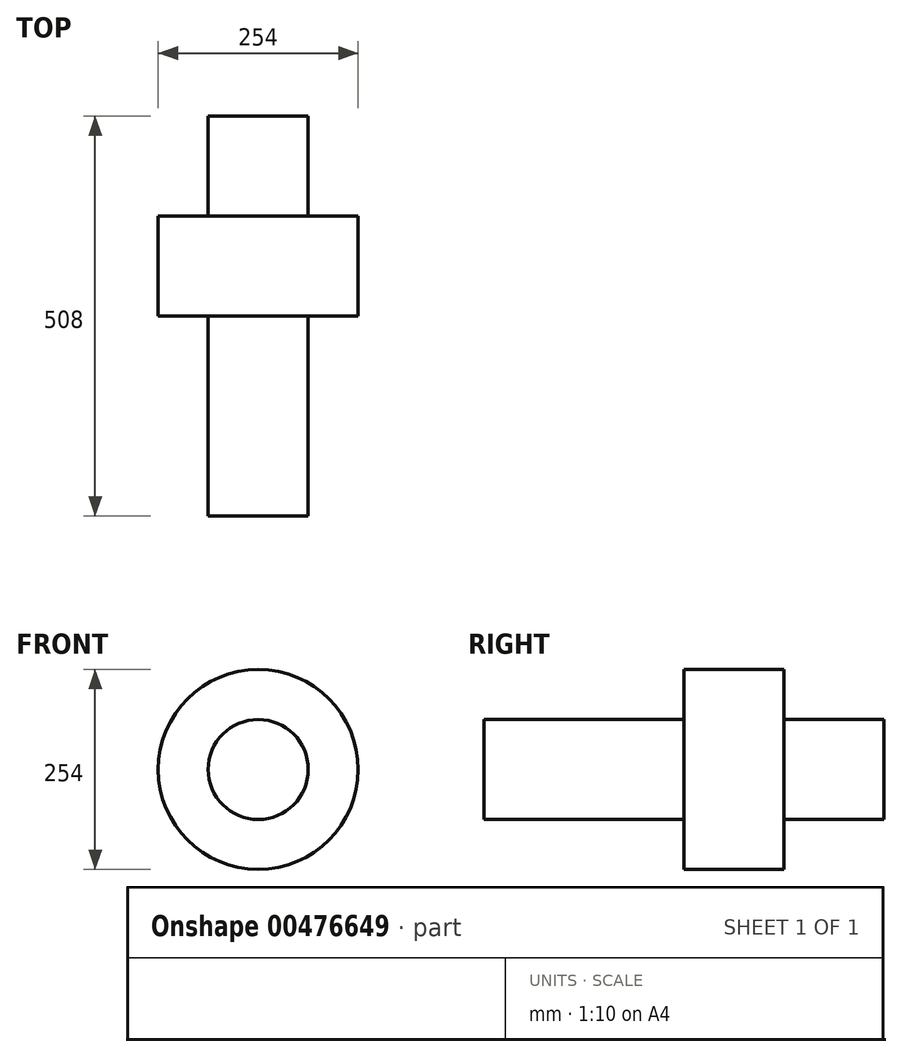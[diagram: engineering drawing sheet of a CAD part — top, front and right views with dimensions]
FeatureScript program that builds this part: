
annotation { "Feature Type Name" : "Feature", "Feature Type Description" : "" }
export const myFeature = defineFeature(function(context is Context, id is Id, definition is map)
    precondition{}
    {
        {
            var Q0;
            Q0=qCreatedBy(makeId("Front.planeOp"),FACE);
            var sketch = newSketch(context, id + "F0", { "sketchPlane" : qUnion([Q0])});
            skCircle(sketch, "E0", {"center": v(0, 0) * mm, "radius": 63.5 * mm});
            skSolve(sketch);
        }
        {
            var Q0;
            Q0 = qSketchRegion(id + "F0", true);
            extrude(context, id + "F1", {"entities" : qUnion([Q0]), "depth" : 508 * mm});
        }
        {
            var Q0;
            Q0=makeQuery(id+"F1.opExtrude","CAP_FACE",FACE,{"disambiguationData":[OSD([sQuery(id+"F0.wireOp",EDGE,"E0")])],"isStart":true});
            cPlane(context, id + "F2", {"entities" : qUnion([Q0]), "cplaneType" : CPlaneType.OFFSET, "offset" : 127 * mm, "oppositeDirection" : true, "width" : 152.4 * mm, "height" : 152.4 * mm});
        }
        {
            var Q0;
            Q0=qCreatedBy(id+"F2.planeOp",FACE);
            var sketch = newSketch(context, id + "F3", { "sketchPlane" : qUnion([Q0])});
            skCircle(sketch, "E1", {"center": v(0, 0) * mm, "radius": 127 * mm});
            skSolve(sketch);
        }
        {
            var Q0;
            Q0 = qSketchRegion(id + "F3", true);
            extrude(context, id + "F4", {"entities" : qUnion([Q0]), "operationType" : NewBodyOperationType.ADD, "oppositeDirection" : true, "depth" : 127 * mm});
        }
    });
